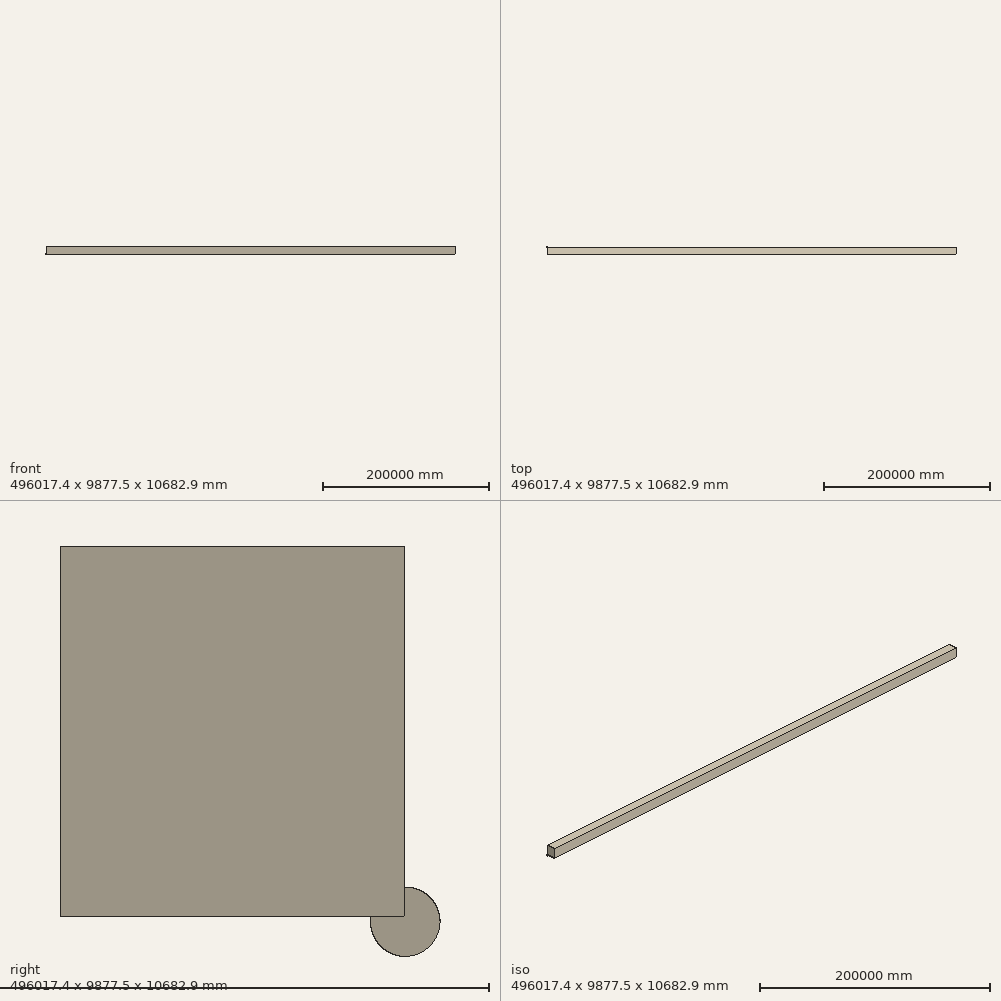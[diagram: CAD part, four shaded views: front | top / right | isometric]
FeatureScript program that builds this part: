
annotation { "Feature Type Name" : "Feature", "Feature Type Description" : "" }
export const myFeature = defineFeature(function(context is Context, id is Id, definition is map)
    precondition{}
    {
        {
            var Q0;
            Q0=qCreatedBy(makeId("Top.planeOp"),FACE);
            var sketch = newSketch(context, id + "F0", { "sketchPlane" : qUnion([Q0])});
            skCircle(sketch, "E0", {"center": v(0, -1.76) * mm, "radius": 35.67 * mm});
            skArc(sketch, "E1", {"start": v(-26.25, 22.4) * mm, "mid": v(-72.99, -54.76) * mm, "end": v(0, -1.76) * mm});
            skArc(sketch, "E2", {"start": v(34.96, 5.3) * mm, "mid": v(42.47, 70.2) * mm, "end": v(-10.72, 32.26) * mm});
            skSolve(sketch);
        }
        {
            var Q0;
            Q0 = qSketchRegion(id + "F0", true);
            extrude(context, id + "F1", {"entities" : qUnion([Q0]), "depth" : 125.73 * mm});
        }
        {
            var Q0;
            Q0=makeQuery(id+"F1.opExtrude","CAP_FACE",FACE,{"disambiguationData":[OSD([sQuery(id+"F0.wireOp",EDGE,"E0"),sQuery(id+"F0.wireOp",EDGE,"E1"),sQuery(id+"F0.wireOp",EDGE,"E2")])],"isStart":false});
            var sketch = newSketch(context, id + "F2", { "sketchPlane" : qUnion([Q0])});
            skSolve(sketch);
        }
        {
            var Q0;
            {var subQ0=sQuery(id+"F0.wireOp",EDGE,"E1");Q0=makeQuery(id+"F2.imprint","IMPRINT",FACE,{"disambiguationData":[TD([[makeQuery(id+"F2.imprint","IMPRINT",EDGE,{"derivedFrom":makeQuery(id+"F1.opExtrude","CAP_EDGE",EDGE,{"disambiguationData":[OSD([subQ0])],"isStart":false})}),1.0]])]});}
            var sketch = newSketch(context, id + "F3", { "sketchPlane" : qUnion([Q0])});
            skCircle(sketch, "E3", {"center": v(0, 0) * mm, "radius": 95.06 * mm});
            skSolve(sketch);
        }
        {
            var Q0;
            Q0 = qSketchRegion(id + "F3", true);
            extrude(context, id + "F4", {"entities" : qUnion([Q0]), "operationType" : NewBodyOperationType.ADD, "depth" : 79.37 * mm});
        }
        {
            var Q0;
            Q0=qCreatedBy(makeId("Right.planeOp"),FACE);
            var sketch = newSketch(context, id + "F5", { "sketchPlane" : qUnion([Q0])});
            skCircle(sketch, "E4", {"center": v(178.43, -24.02) * mm, "radius": 905.23 * mm});
            skSolve(sketch);
        }
        {
            var Q0;
            Q0 = qSketchRegion(id + "F5", true);
            extrude(context, id + "F6", {"entities" : qUnion([Q0]), "operationType" : NewBodyOperationType.ADD, "depth" : 622.3 * mm});
        }
        {
            var Q0;
            Q0=makeQuery(id+"F6.opExtrude","CAP_FACE",FACE,{"disambiguationData":[OSD([sQuery(id+"F5.wireOp",EDGE,"E4")])],"isStart":false});
            var sketch = newSketch(context, id + "F7", { "sketchPlane" : qUnion([Q0])});
            skLineSegment(sketch, "E5.bottom", {"start": v(166.86, 120.37) * mm, "end": v(-8793.84, 120.37) * mm});
            skLineSegment(sketch, "E5.top", {"start": v(166.86, 9753.64) * mm, "end": v(-8793.84, 9753.64) * mm});
            skLineSegment(sketch, "E5.left", {"start": v(166.86, 120.37) * mm, "end": v(166.86, 9753.64) * mm});
            skLineSegment(sketch, "E5.right", {"start": v(-8793.84, 120.37) * mm, "end": v(-8793.84, 9753.64) * mm});
            skSolve(sketch);
        }
        {
            var Q0;
            Q0 = qSketchRegion(id + "F7", true);
            extrude(context, id + "F8", {"entities" : qUnion([Q0]), "operationType" : NewBodyOperationType.ADD, "depth" : 495300 * mm});
        }
    });
